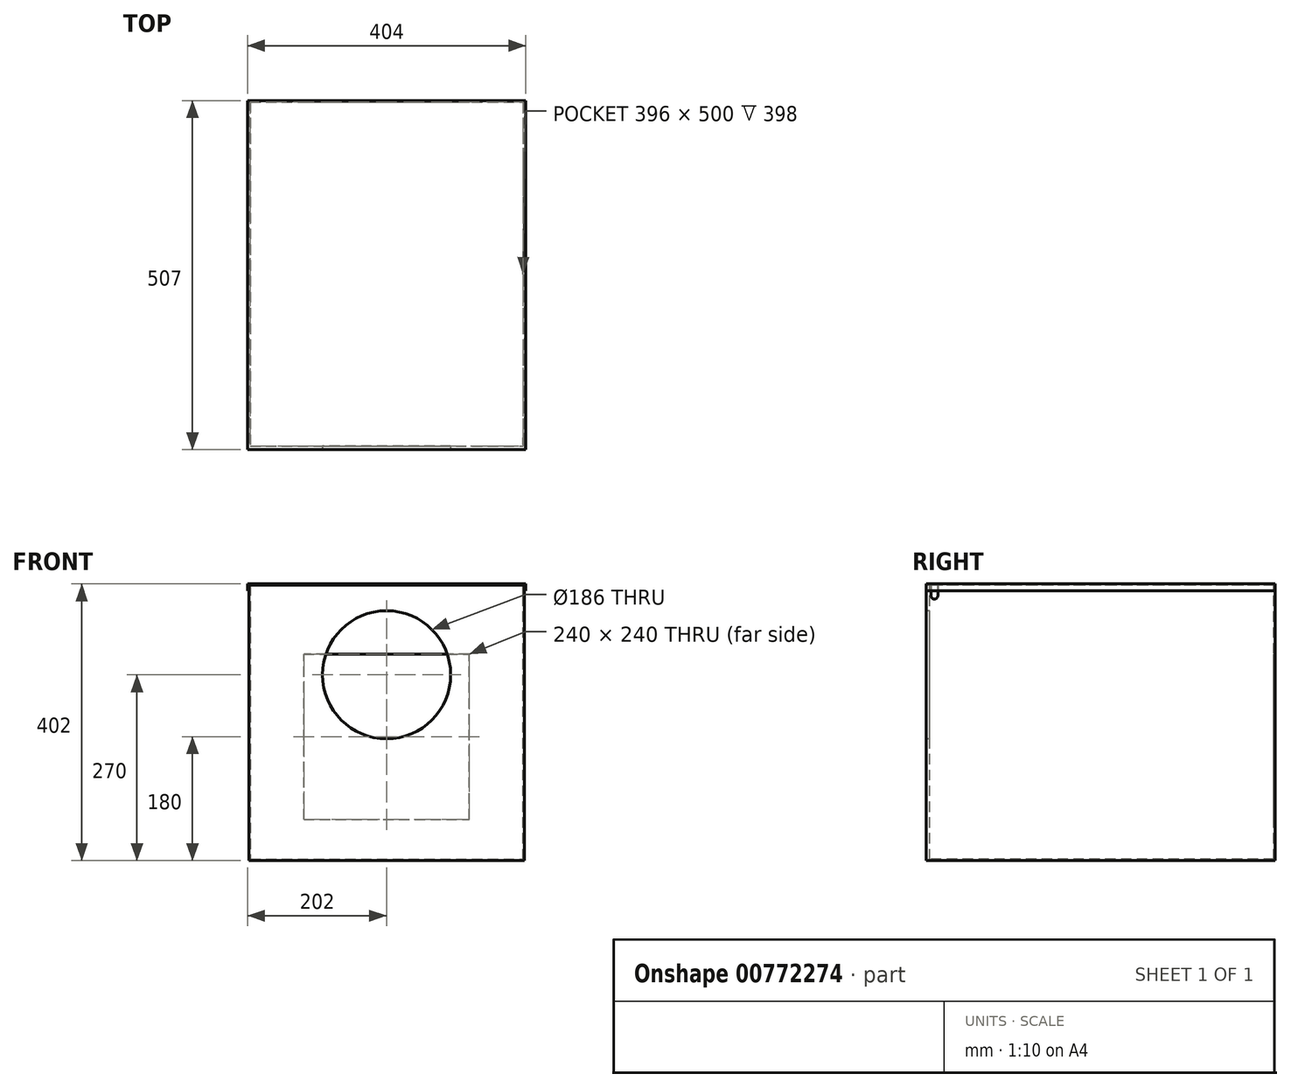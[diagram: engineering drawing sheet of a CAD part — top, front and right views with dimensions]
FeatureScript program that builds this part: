
annotation { "Feature Type Name" : "Feature", "Feature Type Description" : "" }
export const myFeature = defineFeature(function(context is Context, id is Id, definition is map)
    precondition{}
    {
        {
            var Q0;
            Q0=qCreatedBy(makeId("Front.planeOp"),FACE);
            var sketch = newSketch(context, id + "F0", { "sketchPlane" : qUnion([Q0])});
            skLineSegment(sketch, "E0", {"start": v(200, 0) * mm, "end": v(-200, 0) * mm});
            skLineSegment(sketch, "E1", {"start": v(-200, 0) * mm, "end": v(-200, 400) * mm});
            skLineSegment(sketch, "E2", {"start": v(-200, 400) * mm, "end": v(-198, 400) * mm});
            skLineSegment(sketch, "E3", {"start": v(-198, 400) * mm, "end": v(-198, 2) * mm});
            skLineSegment(sketch, "E4", {"start": v(-198, 2) * mm, "end": v(198, 2) * mm});
            skLineSegment(sketch, "E5", {"start": v(198, 2) * mm, "end": v(198, 400) * mm});
            skLineSegment(sketch, "E6", {"start": v(198, 400) * mm, "end": v(200, 400) * mm});
            skLineSegment(sketch, "E7", {"start": v(200, 400) * mm, "end": v(200, 0) * mm});
            skSolve(sketch);
        }
        {
            var Q0;
            Q0 = qSketchRegion(id + "F0", true);
            extrude(context, id + "F1", {"entities" : qUnion([Q0]), "oppositeDirection" : true, "depth" : 500 * mm, "offsetDistance" : 25 * mm});
        }
        {
            var Q0;
            Q0=makeQuery(id+"F1.opExtrude","CAP_FACE",FACE,{"disambiguationData":[OSD([sQuery(id+"F0.wireOp",EDGE,"E0"),sQuery(id+"F0.wireOp",EDGE,"E1"),sQuery(id+"F0.wireOp",EDGE,"E2"),sQuery(id+"F0.wireOp",EDGE,"E3"),sQuery(id+"F0.wireOp",EDGE,"E4"),sQuery(id+"F0.wireOp",EDGE,"E5"),sQuery(id+"F0.wireOp",EDGE,"E6"),sQuery(id+"F0.wireOp",EDGE,"E7")])],"isStart":true});
            var sketch = newSketch(context, id + "F2", { "sketchPlane" : qUnion([Q0])});
            skLineSegment(sketch, "E8.0", {"start": v(200, 400) * mm, "end": v(200, 0) * mm});
            skLineSegment(sketch, "E8.1", {"start": v(200, 0) * mm, "end": v(-200, 0) * mm});
            skLineSegment(sketch, "E8.2", {"start": v(-200, 0) * mm, "end": v(-200, 400) * mm});
            skLineSegment(sketch, "E9", {"start": v(-200, 400) * mm, "end": v(200, 400) * mm});
            skSolve(sketch);
        }
        {
            var Q0;
            Q0 = qSketchRegion(id + "F2", true);
            extrude(context, id + "F3", {"entities" : qUnion([Q0]), "operationType" : NewBodyOperationType.ADD, "depth" : 5 * mm, "offsetDistance" : 25 * mm});
        }
        {
            var Q0;
            Q0=makeQuery(id+"F3.opExtrude","CAP_FACE",FACE,{"disambiguationData":[OSD([sQuery(id+"F2.wireOp",EDGE,"E8.0"),sQuery(id+"F2.wireOp",EDGE,"E8.1"),sQuery(id+"F2.wireOp",EDGE,"E8.2"),sQuery(id+"F2.wireOp",EDGE,"E9")])],"isStart":false});
            var sketch = newSketch(context, id + "F4", { "sketchPlane" : qUnion([Q0])});
            skCircle(sketch, "E10", {"center": v(0, 270) * mm, "radius": 93 * mm});
            skSolve(sketch);
        }
        {
            var Q0;
            Q0 = qSketchRegion(id + "F4", true);
            extrude(context, id + "F5", {"entities" : qUnion([Q0]), "operationType" : NewBodyOperationType.REMOVE, "endBound" : BoundingType.UP_TO_NEXT, "oppositeDirection" : true, "depth" : 25 * mm, "offsetDistance" : 25 * mm});
        }
        {
            var Q0;
            {var subQ0=makeQuery(id+"F3.boolean.opBoolean","MERGE",FACE,{"derivedFrom":[makeQuery(id+"F1.opExtrude","SWEPT_FACE",FACE,{"disambiguationData":[OSD([sQuery(id+"F0.wireOp",EDGE,"E7")])]}),makeQuery(id+"F3.opExtrude","SWEPT_FACE",FACE,{"disambiguationData":[OSD([sQuery(id+"F2.wireOp",EDGE,"E8.0")])]})]});Q0=makeQuery(id+"F0WVTyklOvh4qti_1.boolean.opBoolean","MERGE",FACE,{"derivedFrom":[subQ0,makeQuery(id+"F0WVTyklOvh4qti_1.opPattern","COPY",FACE,{"derivedFrom":subQ0,"instanceName":"1"})]});}
            var sketch = newSketch(context, id + "F6", { "sketchPlane" : qUnion([Q0])});
            skLineSegment(sketch, "E11.bottom", {"start": v(2, 400) * mm, "end": v(12, 400) * mm});
            skLineSegment(sketch, "E11.top", {"start": v(7, 380) * mm, "end": v(7, 380) * mm});
            skLineSegment(sketch, "E11.left", {"start": v(2, 400) * mm, "end": v(2, 385) * mm});
            skLineSegment(sketch, "E11.right", {"start": v(12, 400) * mm, "end": v(12, 385) * mm});
            skPoint(sketch, "E12.visualSharp", {"position": v(12, 380) * mm});
            skArc(sketch, "E12.filletArc", {"start": v(7, 380) * mm, "mid": v(10.54, 381.46) * mm, "end": v(12, 385) * mm});
            skPoint(sketch, "E13.visualSharp", {"position": v(2, 380) * mm});
            skArc(sketch, "E13.filletArc", {"start": v(2, 385) * mm, "mid": v(3.46, 381.46) * mm, "end": v(7, 380) * mm});
            skSolve(sketch);
        }
        {
            var Q0;
            Q0 = qSketchRegion(id + "F6", true);
            extrude(context, id + "F7", {"entities" : qUnion([Q0]), "operationType" : NewBodyOperationType.REMOVE, "endBound" : BoundingType.UP_TO_NEXT, "oppositeDirection" : true, "depth" : 25 * mm, "offsetDistance" : 25 * mm});
        }
        {
            var Q0;
            Q0=makeQuery(id+"F1.opExtrude","CAP_FACE",FACE,{"disambiguationData":[OSD([sQuery(id+"F0.wireOp",EDGE,"E0"),sQuery(id+"F0.wireOp",EDGE,"E1"),sQuery(id+"F0.wireOp",EDGE,"E2"),sQuery(id+"F0.wireOp",EDGE,"E3"),sQuery(id+"F0.wireOp",EDGE,"E4"),sQuery(id+"F0.wireOp",EDGE,"E5"),sQuery(id+"F0.wireOp",EDGE,"E6"),sQuery(id+"F0.wireOp",EDGE,"E7")])],"isStart":false});
            var sketch = newSketch(context, id + "F8", { "sketchPlane" : qUnion([Q0])});
            skLineSegment(sketch, "E14.0", {"start": v(200, 0) * mm, "end": v(200, 400) * mm});
            skLineSegment(sketch, "E14.1", {"start": v(-200, 0) * mm, "end": v(200, 0) * mm});
            skLineSegment(sketch, "E14.2", {"start": v(-200, 400) * mm, "end": v(-200, 0) * mm});
            skLineSegment(sketch, "E15", {"start": v(-200, 400) * mm, "end": v(200, 400) * mm});
            skSolve(sketch);
        }
        {
            var Q0;
            Q0 = qSketchRegion(id + "F8", true);
            extrude(context, id + "F9", {"entities" : qUnion([Q0]), "operationType" : NewBodyOperationType.ADD, "depth" : 2 * mm, "offsetDistance" : 25 * mm});
        }
        {
            var Q0;
            Q0=makeQuery(id+"F9.opExtrude","CAP_FACE",FACE,{"disambiguationData":[OSD([sQuery(id+"F8.wireOp",EDGE,"E14.0"),sQuery(id+"F8.wireOp",EDGE,"E14.1"),sQuery(id+"F8.wireOp",EDGE,"E14.2"),sQuery(id+"F8.wireOp",EDGE,"E15")])],"isStart":false});
            var sketch = newSketch(context, id + "F10", { "sketchPlane" : qUnion([Q0])});
            skLineSegment(sketch, "E16.bottom", {"start": v(-120, 300) * mm, "end": v(120, 300) * mm});
            skLineSegment(sketch, "E16.top", {"start": v(-120, 60) * mm, "end": v(120, 60) * mm});
            skLineSegment(sketch, "E16.left", {"start": v(-120, 300) * mm, "end": v(-120, 60) * mm});
            skLineSegment(sketch, "E16.right", {"start": v(120, 300) * mm, "end": v(120, 60) * mm});
            skSolve(sketch);
        }
        {
            var Q0;
            Q0 = qSketchRegion(id + "F10", true);
            extrude(context, id + "F11", {"entities" : qUnion([Q0]), "operationType" : NewBodyOperationType.REMOVE, "endBound" : BoundingType.UP_TO_NEXT, "oppositeDirection" : true, "depth" : 25 * mm, "offsetDistance" : 25 * mm});
        }
        {
            var Q0;
            Q0=makeQuery(id+"F3.opExtrude","CAP_FACE",FACE,{"disambiguationData":[OSD([sQuery(id+"F2.wireOp",EDGE,"E8.0"),sQuery(id+"F2.wireOp",EDGE,"E8.1"),sQuery(id+"F2.wireOp",EDGE,"E8.2"),sQuery(id+"F2.wireOp",EDGE,"E9")])],"isStart":false});
            var sketch = newSketch(context, id + "F12", { "sketchPlane" : qUnion([Q0])});
            skLineSegment(sketch, "E17", {"start": v(-200, 400) * mm, "end": v(-200, 392) * mm});
            skLineSegment(sketch, "E18", {"start": v(-200, 392) * mm, "end": v(-202, 392) * mm});
            skLineSegment(sketch, "E19", {"start": v(-202, 392) * mm, "end": v(-202, 402) * mm});
            skLineSegment(sketch, "E20", {"start": v(-202, 402) * mm, "end": v(202, 402) * mm});
            skLineSegment(sketch, "E21", {"start": v(202, 402) * mm, "end": v(202, 392) * mm});
            skLineSegment(sketch, "E22", {"start": v(202, 392) * mm, "end": v(200, 392) * mm});
            skLineSegment(sketch, "E23", {"start": v(200, 392) * mm, "end": v(200, 400) * mm});
            skLineSegment(sketch, "E24", {"start": v(200, 400) * mm, "end": v(-200, 400) * mm});
            skSolve(sketch);
        }
        {
            var Q0;
            Q0 = qSketchRegion(id + "F12", true);
            var Q1;
            Q1=makeQuery(id+"F9.opExtrude","CAP_FACE",FACE,{"disambiguationData":[OSD([sQuery(id+"F8.wireOp",EDGE,"E14.0"),sQuery(id+"F8.wireOp",EDGE,"E14.1"),sQuery(id+"F8.wireOp",EDGE,"E14.2"),sQuery(id+"F8.wireOp",EDGE,"E15")])],"isStart":false});
            extrude(context, id + "F13", {"entities" : qUnion([Q0]), "endBound" : BoundingType.UP_TO_SURFACE, "oppositeDirection" : true, "depth" : 500 * mm, "endBoundEntityFace" : qUnion([Q1]), "offsetDistance" : 25 * mm});
        }
    });
